# Revit family: VLN_Nim-II-Mes-E_F3049_BIM_NL
name_source: partatom
category: Plumbing Fixtures
revit_build: Autodesk Revit MEP 2014 (Build: 20130308_1515(x64)
units: mm (PartAtom-declared; Revit-internal decimal feet)

## types (1)
- F3049AA - NIM-II-MES-E TOILETKRAAN DR UITL 200 CHR
    Accessories = www.idealstandardnederland.nl
    AreaUnits = millimeters
    Assembly Code = C1030200
    AssetType = Vast
    BIMObjectName = VLN_Venlo_SinkTaps_F3049AA
    BREEAMApproved = No
    BarCode = 8711678062871
    Brand = Venlo
    CWFU = 0
    CodePerformance = EN 817, DIN 4109
    Color = Chroom
    ConnectionType = Sanitair
    Cost = 0 $
    Default Elevation = 800 mm  [stored 2.62467 ft]
    Description = Venlo Nimbus II Messing toiletkraan eco. Koud. Hoog. Draaibare uitloop. Straalregelaar. Sprong 200 mm. Hoogte uitloop 185 mm. Eco bovendeel. Koppeling 12 mm.
    DurationUnit = jaar
    ECA = No
    ExpectedLife = 25
    FaucetFunction = Toiletkraan
    FaucetOperation = Eengreeps
    FaucetType = Toiletkraan
    Features = Toiletkraan eco. Koud. Hoog. Draaibare uitloop. Straalregelaar. Sprong 200 mm. Hoogte uitloop 185 mm. Eco bovendeel. Koppeling 12 mm.
    Finish = Chroom
    FlowRate = 8,3 liter @ 3 bar
    HWFU = 0
    IfcExportAs = IfcValveType
    IfcExportType = FAUCET
    InstallationInstructions = http://www.idealstandardnederland.nl
    LinearUnits = millimeters
    ManufacturerURL = www.idealstandardnederland.nl
    Material = Messing
    Model = F3049AA
    ModelNumber = F3049AA
    ModelReference = Venlo Nimbus II Messing toiletkraan eco. Koud. Hoog. Draaibare uitloop. Straalregelaar. Sprong 200 mm. Hoogte uitloop 185 mm. Eco bovendeel. Koppeling 12 mm.
    NBSDescription = Water supply fittings for sinks
    NBSReference = 45-35-70/345
    Name = SinkTaps_F3049AA_Venlo
    NettWeight = 0.853 kg
    NominalHeight = 296 mm
    NominalLength = 238 mm
    NominalWidth = 95 mm
    ProductInformation = http://www.idealstandardnederland.nl
    Shape = Gesculptuurd
    Size = 95 x 238 x 296 mm
    Space = Internal
    SpareParts = www.idealstandardnederland.nl
    TMV3 = Yes
    TestPressure = 10 Bar
    URL = www.idealstandardnederland.nl
    Uniclass2015Code = Pr_40_20_87_84
    Uniclass2015Title = Sink taps
    Uniclass2015Version = Products v1.1
    ValveMechanism = Keramische schijven
    ValveOperation = Eengreeps
    Version = 1
    VolumeUnits = liter
    WFU = 0
    WRAS = No
    WarrantyDescription = Fabrieksgarantie
    WarrantyDurationParts = 10
    WarrantyDurationUnit = jaar
    WaterEfficientProduct = No
    WorkingPressure = 1-5 bar

note: [stored X ft] marks values corroborated as IEEE doubles in the binary element streams (Revit-internal decimal feet)

## geometry (parser evidence)
native form markers: Sweep x1
no freeform markers — native parametric forms only
